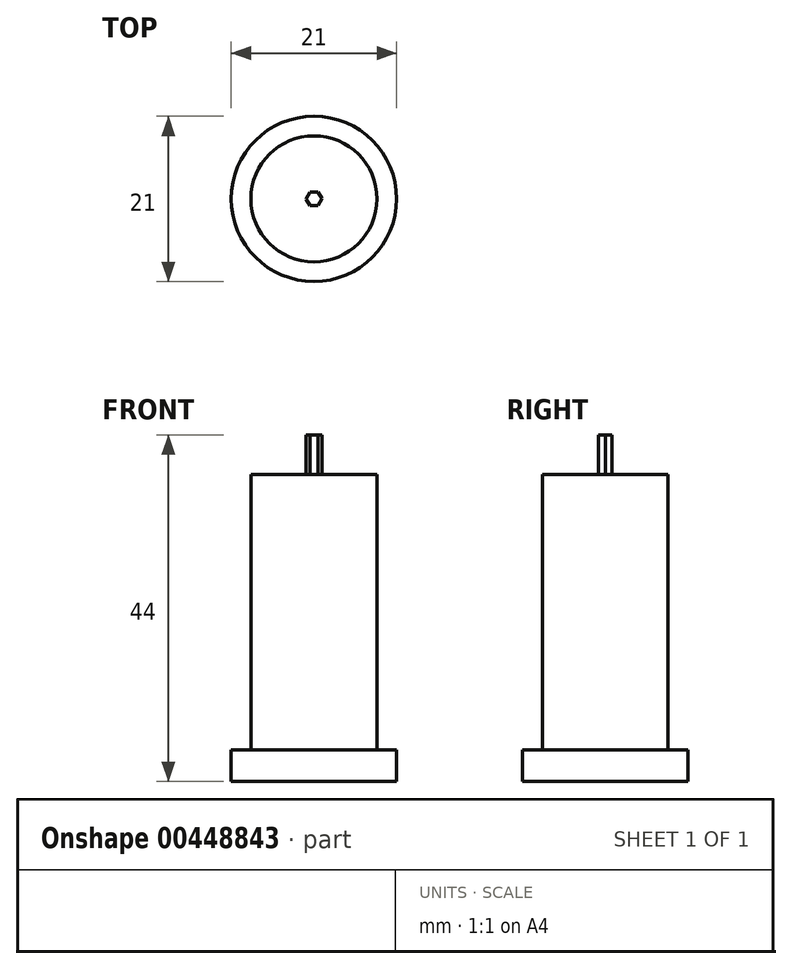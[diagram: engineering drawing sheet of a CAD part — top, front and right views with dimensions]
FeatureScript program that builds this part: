
annotation { "Feature Type Name" : "Feature", "Feature Type Description" : "" }
export const myFeature = defineFeature(function(context is Context, id is Id, definition is map)
    precondition{}
    {
        {
            var Q0;
            Q0=qCreatedBy(makeId("Top.planeOp"),FACE);
            var sketch = newSketch(context, id + "F0", { "sketchPlane" : qUnion([Q0])});
            skCircle(sketch, "E0", {"center": v(0, 0) * mm, "radius": 10.5 * mm});
            skSolve(sketch);
        }
        {
            var Q0;
            Q0=qSketchRegion(id+"F0",true);
            extrude(context, id + "F1", {"entities" : qUnion([Q0]), "depth" : 4 * mm});
        }
        {
            var Q0;
            Q0=qCreatedBy(makeId("Top.planeOp"),FACE);
            var sketch = newSketch(context, id + "F2", { "sketchPlane" : qUnion([Q0])});
            skCircle(sketch, "E1", {"center": v(0, 0) * mm, "radius": 8 * mm});
            skSolve(sketch);
        }
        {
            var Q0;
            Q0=qSketchRegion(id+"F2",true);
            extrude(context, id + "F3", {"entities" : qUnion([Q0]), "operationType" : NewBodyOperationType.ADD, "depth" : 39 * mm});
        }
        {
            var Q0;
            Q0=makeQuery(id+"F3.opExtrude","CAP_FACE",FACE,{"disambiguationData":[OSD([sQuery(id+"F2.wireOp",EDGE,"E1")])],"isStart":false});
            var sketch = newSketch(context, id + "F4", { "sketchPlane" : qUnion([Q0])});
            skCircle(sketch, "E2.cCircle", {"center": v(0, 0) * mm, "radius": 0.87 * mm, "construction": true});
            skLineSegment(sketch, "E2.0", {"start": v(1, 0) * mm, "end": v(0.5, -0.86) * mm});
            skLineSegment(sketch, "E2.1", {"start": v(0.5, -0.86) * mm, "end": v(-0.5, -0.87) * mm});
            skLineSegment(sketch, "E2.2", {"start": v(-0.5, -0.87) * mm, "end": v(-1, 0) * mm});
            skLineSegment(sketch, "E2.3", {"start": v(-1, 0) * mm, "end": v(-0.5, 0.86) * mm});
            skLineSegment(sketch, "E2.4", {"start": v(-0.5, 0.86) * mm, "end": v(0.5, 0.87) * mm});
            skLineSegment(sketch, "E2.5", {"start": v(0.5, 0.87) * mm, "end": v(1, 0) * mm});
            skPoint(sketch, "E2.0.midPoint", {"position": v(0.75, -0.43) * mm});
            skSolve(sketch);
        }
        {
            var Q0;
            Q0 = qSketchRegion(id + "F4", true);
            extrude(context, id + "F5", {"entities" : qUnion([Q0]), "operationType" : NewBodyOperationType.ADD, "depth" : 5 * mm});
        }
    });
